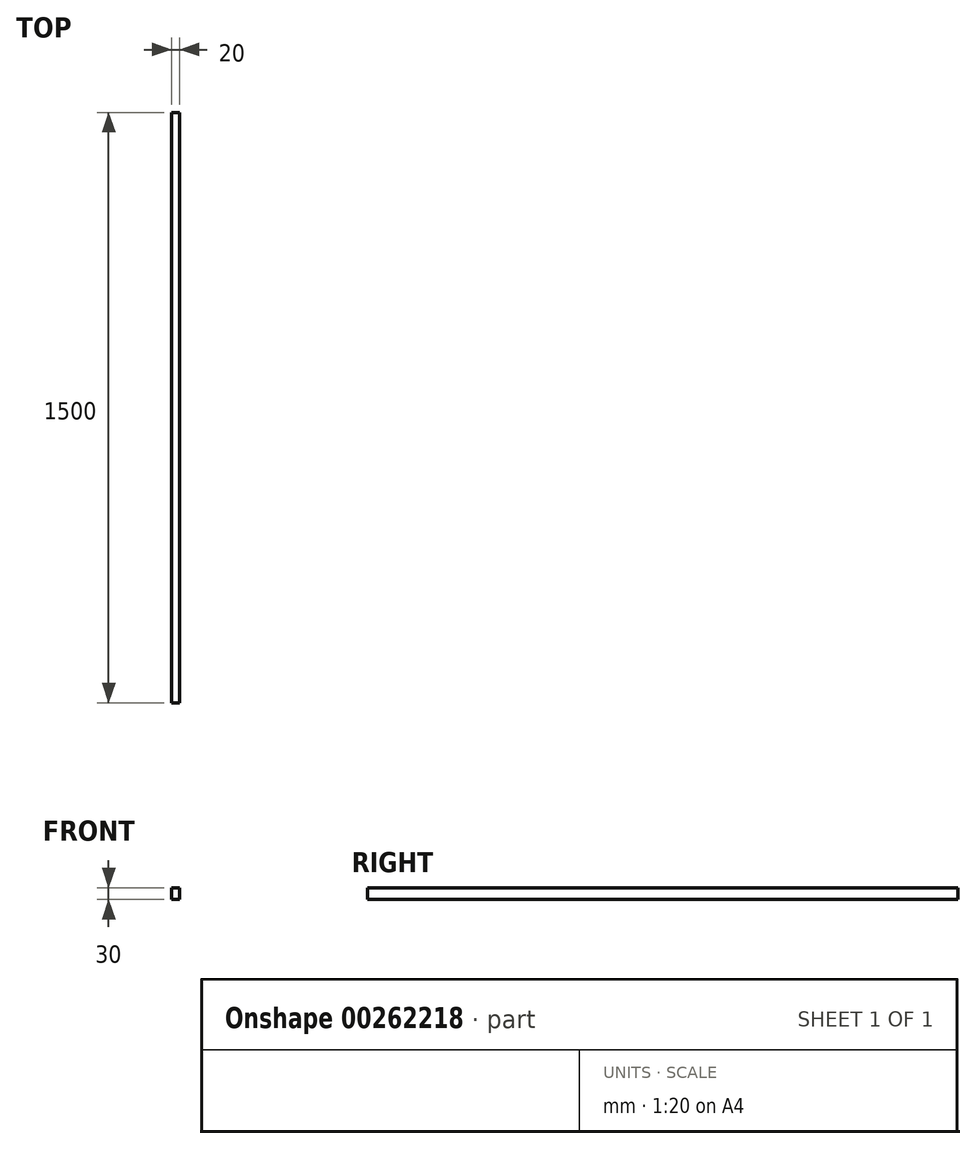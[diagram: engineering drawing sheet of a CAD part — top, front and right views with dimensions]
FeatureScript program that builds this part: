
annotation { "Feature Type Name" : "Feature", "Feature Type Description" : "" }
export const myFeature = defineFeature(function(context is Context, id is Id, definition is map)
    precondition{}
    {
        {
            var Q0;
            Q0=qCreatedBy(makeId("Front.planeOp"),FACE);
            var sketch = newSketch(context, id + "F0", { "sketchPlane" : qUnion([Q0])});
            skLineSegment(sketch, "E0.bottom", {"start": v(10, 15) * mm, "end": v(-10, 15) * mm});
            skLineSegment(sketch, "E0.top", {"start": v(10, -15) * mm, "end": v(-10, -15) * mm});
            skLineSegment(sketch, "E0.left", {"start": v(10, 15) * mm, "end": v(10, -15) * mm});
            skLineSegment(sketch, "E0.right", {"start": v(-10, 15) * mm, "end": v(-10, -15) * mm});
            skPoint(sketch, "E0.middle", {"position": v(0, 0) * mm});
            skSolve(sketch);
        }
        {
            var Q0;
            Q0=makeQuery(id+"F0.imprint","IMPRINT",FACE,{"disambiguationData":[TD([[makeQuery(id+"F0.imprint","IMPRINT",EDGE,{"derivedFrom":sQuery(id+"F0.wireOp",EDGE,"E0.bottom")}),1.0]])]});
            extrude(context, id + "F1", {"entities" : qUnion([Q0]), "depth" : 1500 * mm, "offsetDistance" : 25 * mm});
        }
    });
